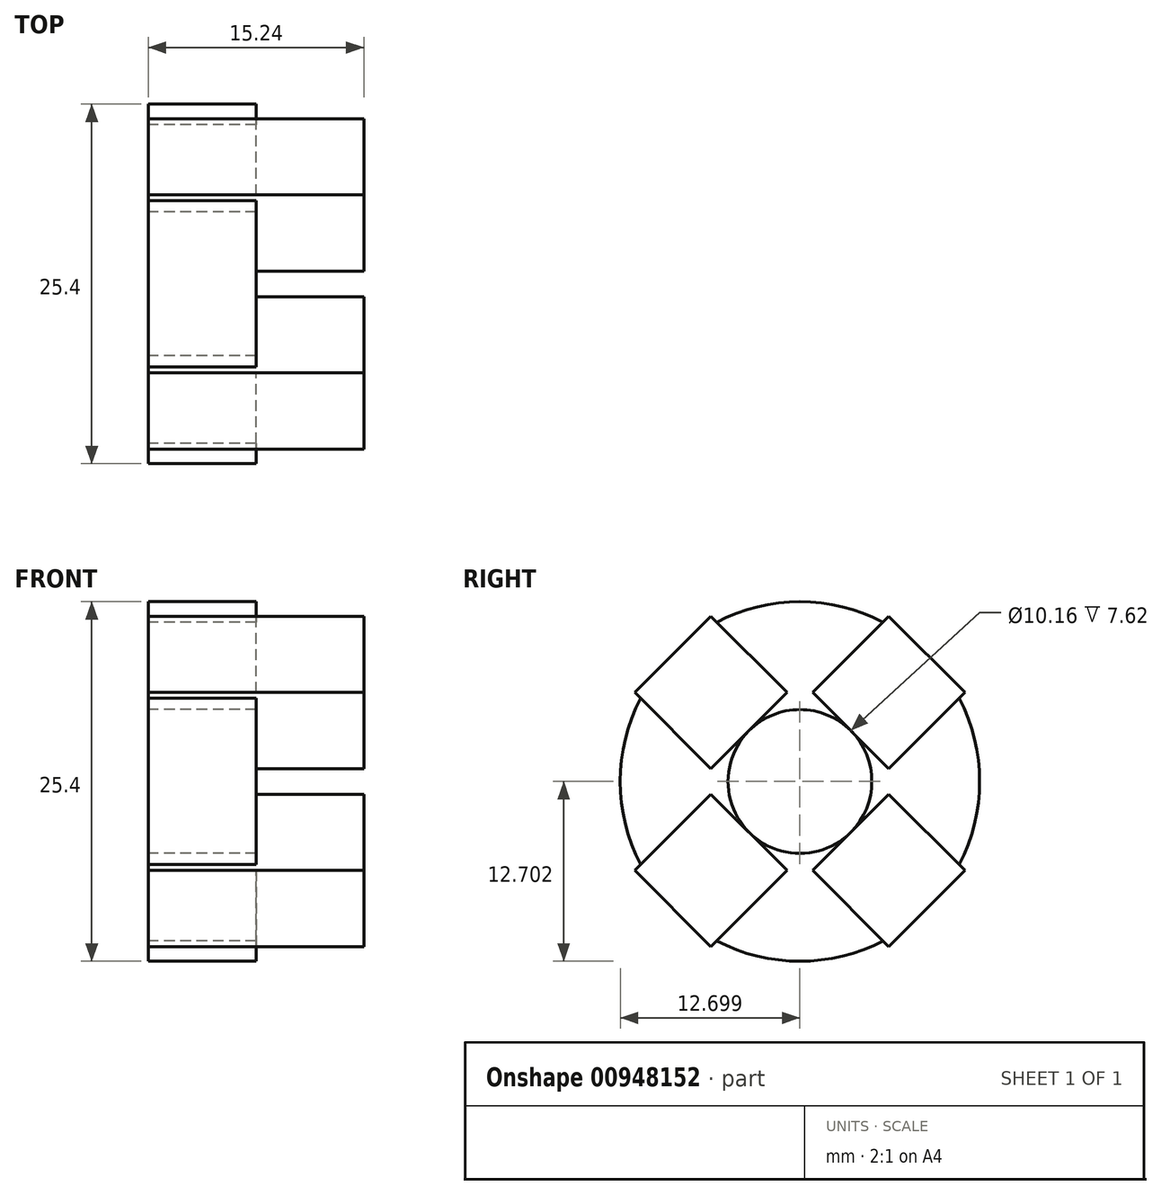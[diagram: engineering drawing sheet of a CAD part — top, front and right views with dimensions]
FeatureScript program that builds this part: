
annotation { "Feature Type Name" : "Feature", "Feature Type Description" : "" }
export const myFeature = defineFeature(function(context is Context, id is Id, definition is map)
    precondition{}
    {
        {
            var Q0;
            Q0=qCreatedBy(makeId("Right.planeOp"),FACE);
            var sketch = newSketch(context, id + "F0", { "sketchPlane" : qUnion([Q0])});
            skCircle(sketch, "E0", {"center": v(-34.03, 25.2) * mm, "radius": 12.7 * mm});
            skCircle(sketch, "E1", {"center": v(-34.03, 25.2) * mm, "radius": 5.08 * mm});
            skLineSegment(sketch, "E2.bottom", {"start": v(-25.05, 34.17) * mm, "end": v(-43.01, 34.17) * mm});
            skLineSegment(sketch, "E2.top", {"start": v(-25.05, 16.21) * mm, "end": v(-43.01, 16.21) * mm});
            skLineSegment(sketch, "E2.left", {"start": v(-25.05, 34.17) * mm, "end": v(-25.05, 16.21) * mm});
            skLineSegment(sketch, "E2.right", {"start": v(-43.01, 34.17) * mm, "end": v(-43.01, 16.21) * mm});
            skLineSegment(sketch, "E3", {"start": v(-27.74, 36.87) * mm, "end": v(-33.13, 31.48) * mm});
            skLineSegment(sketch, "E4", {"start": v(-33.13, 31.48) * mm, "end": v(-27.74, 26.09) * mm});
            skLineSegment(sketch, "E5", {"start": v(-27.74, 26.09) * mm, "end": v(-22.36, 31.48) * mm});
            skLineSegment(sketch, "E6", {"start": v(-22.36, 18.9) * mm, "end": v(-27.74, 24.3) * mm});
            skLineSegment(sketch, "E7", {"start": v(-27.74, 24.3) * mm, "end": v(-33.13, 18.9) * mm});
            skLineSegment(sketch, "E8", {"start": v(-33.13, 18.9) * mm, "end": v(-27.74, 13.53) * mm});
            skLineSegment(sketch, "E9", {"start": v(-40.32, 36.87) * mm, "end": v(-34.93, 31.48) * mm});
            skLineSegment(sketch, "E10", {"start": v(-34.93, 31.48) * mm, "end": v(-40.32, 26.09) * mm});
            skLineSegment(sketch, "E11", {"start": v(-40.32, 26.09) * mm, "end": v(-45.7, 31.48) * mm});
            skLineSegment(sketch, "E12", {"start": v(-27.74, 36.87) * mm, "end": v(-22.36, 31.48) * mm});
            skLineSegment(sketch, "E13", {"start": v(-40.32, 36.87) * mm, "end": v(-45.7, 31.48) * mm});
            skLineSegment(sketch, "E14", {"start": v(-22.36, 18.9) * mm, "end": v(-27.74, 13.53) * mm});
            skLineSegment(sketch, "E15", {"start": v(-40.33, 13.53) * mm, "end": v(-34.95, 18.9) * mm});
            skLineSegment(sketch, "E16", {"start": v(-34.95, 18.9) * mm, "end": v(-40.33, 24.29) * mm});
            skLineSegment(sketch, "E17", {"start": v(-40.33, 24.29) * mm, "end": v(-45.7, 18.9) * mm});
            skLineSegment(sketch, "E18", {"start": v(-45.7, 18.9) * mm, "end": v(-40.33, 13.53) * mm});
            skSolve(sketch);
        }
        {
            var Q0;
            {var subQ0=sQuery(id+"F0.wireOp",EDGE,"E3");var subQ1=sQuery(id+"F0.wireOp",EDGE,"E0");var subQ2=makeQuery(id+"F0.imprint","INTERSECT",VERTEX,{"derivedFrom":[subQ1,subQ0]});Q0=makeQuery(id+"F0.imprint","IMPRINT",FACE,{"disambiguationData":[TD([[makeQuery(id+"F0.imprint","IMPRINT",EDGE,{"disambiguationData":[TD([[subQ2,-1.0]])],"derivedFrom":subQ1}),1.0]])]});}
            var Q1;
            {var subQ7=sQuery(id+"F0.wireOp",EDGE,"E1");var subQ9=sQuery(id+"F0.wireOp",EDGE,"E10");var subQ10=makeQuery(id+"F0.imprint","INTERSECT",VERTEX,{"derivedFrom":[subQ7,subQ9]});Q1=makeQuery(id+"F0.imprint","IMPRINT",FACE,{"disambiguationData":[TD([[makeQuery(id+"F0.imprint","IMPRINT",EDGE,{"disambiguationData":[TD([[subQ10,1.0]])],"derivedFrom":subQ7}),-1.0]])]});}
            var Q2;
            {var subQ0=sQuery(id+"F0.wireOp",EDGE,"E11");var subQ1=sQuery(id+"F0.wireOp",EDGE,"E0");var subQ2=makeQuery(id+"F0.imprint","INTERSECT",VERTEX,{"derivedFrom":[subQ1,subQ0]});Q2=makeQuery(id+"F0.imprint","IMPRINT",FACE,{"disambiguationData":[TD([[makeQuery(id+"F0.imprint","IMPRINT",EDGE,{"disambiguationData":[TD([[subQ2,-1.0]])],"derivedFrom":subQ1}),1.0]])]});}
            var Q3;
            {var subQ17=sQuery(id+"F0.wireOp",EDGE,"E16");Q3=makeQuery(id+"F0.imprint","IMPRINT",FACE,{"disambiguationData":[TD([[makeQuery(id+"F0.imprint","IMPRINT",EDGE,{"derivedFrom":subQ17}),-1.0]])]});}
            var Q4;
            {var subQ1=sQuery(id+"F0.wireOp",EDGE,"E4");var subQ3=sQuery(id+"F0.wireOp",EDGE,"E1");var subQ4=makeQuery(id+"F0.imprint","INTERSECT",VERTEX,{"derivedFrom":[subQ3,subQ1]});Q4=makeQuery(id+"F0.imprint","IMPRINT",FACE,{"disambiguationData":[TD([[makeQuery(id+"F0.imprint","IMPRINT",EDGE,{"disambiguationData":[TD([[subQ4,1.0]])],"derivedFrom":subQ3}),-1.0]])]});}
            var Q5;
            {var subQ0=sQuery(id+"F0.wireOp",EDGE,"E5");var subQ1=sQuery(id+"F0.wireOp",EDGE,"E0");var subQ2=makeQuery(id+"F0.imprint","INTERSECT",VERTEX,{"derivedFrom":[subQ1,subQ0]});Q5=makeQuery(id+"F0.imprint","IMPRINT",FACE,{"disambiguationData":[TD([[makeQuery(id+"F0.imprint","IMPRINT",EDGE,{"disambiguationData":[TD([[subQ2,1.0]])],"derivedFrom":subQ1}),1.0]])]});}
            var Q6;
            {var subQ0=sQuery(id+"F0.wireOp",EDGE,"E15");var subQ1=sQuery(id+"F0.wireOp",EDGE,"E0");var subQ2=makeQuery(id+"F0.imprint","INTERSECT",VERTEX,{"derivedFrom":[subQ1,subQ0]});Q6=makeQuery(id+"F0.imprint","IMPRINT",FACE,{"disambiguationData":[TD([[makeQuery(id+"F0.imprint","IMPRINT",EDGE,{"disambiguationData":[TD([[subQ2,-1.0]])],"derivedFrom":subQ1}),1.0]])]});}
            var Q7;
            {var subQ0=sQuery(id+"F0.wireOp",EDGE,"E10");var subQ1=sQuery(id+"F0.wireOp",EDGE,"E9");var subQ2=makeQuery(id+"F0.imprint","INTERSECT",VERTEX,{"derivedFrom":[subQ1,subQ0]});Q7=makeQuery(id+"F0.imprint","IMPRINT",FACE,{"disambiguationData":[TD([[makeQuery(id+"F0.imprint","IMPRINT",EDGE,{"disambiguationData":[TD([[subQ2,1.0]])],"derivedFrom":subQ1}),-1.0]])]});}
            var Q8;
            {var subQ0=sQuery(id+"F0.wireOp",EDGE,"E13");var subQ1=sQuery(id+"F0.wireOp",EDGE,"E0");var subQ2=makeQuery(id+"F0.imprint","INTERSECT",VERTEX,{"derivedFrom":[subQ1,subQ0]});Q8=makeQuery(id+"F0.imprint","IMPRINT",FACE,{"disambiguationData":[TD([[makeQuery(id+"F0.imprint","IMPRINT",EDGE,{"disambiguationData":[TD([[subQ2,1.0]])],"derivedFrom":subQ1}),1.0]])]});}
            var Q9;
            {var subQ1=sQuery(id+"F0.wireOp",EDGE,"E0");var subQ3=sQuery(id+"F0.wireOp",EDGE,"E11");var subQ4=makeQuery(id+"F0.imprint","INTERSECT",VERTEX,{"derivedFrom":[subQ1,subQ3]});Q9=makeQuery(id+"F0.imprint","IMPRINT",FACE,{"disambiguationData":[TD([[makeQuery(id+"F0.imprint","IMPRINT",EDGE,{"disambiguationData":[TD([[subQ4,1.0]])],"derivedFrom":subQ3}),-1.0]])]});}
            var Q10;
            {var subQ6=sQuery(id+"F0.wireOp",EDGE,"E14");var subQ8=sQuery(id+"F0.wireOp",EDGE,"E2.top");var subQ9=makeQuery(id+"F0.imprint","INTERSECT",VERTEX,{"derivedFrom":[subQ8,subQ6]});Q10=makeQuery(id+"F0.imprint","IMPRINT",FACE,{"disambiguationData":[TD([[makeQuery(id+"F0.imprint","IMPRINT",EDGE,{"disambiguationData":[TD([[subQ9,-1.0]])],"derivedFrom":subQ8}),-1.0]])]});}
            var Q11;
            {var subQ0=sQuery(id+"F0.wireOp",EDGE,"E14");var subQ1=sQuery(id+"F0.wireOp",EDGE,"E0");var subQ2=makeQuery(id+"F0.imprint","INTERSECT",VERTEX,{"disambiguationData":[OD(1.0)],"derivedFrom":[subQ1,subQ0]});Q11=makeQuery(id+"F0.imprint","IMPRINT",FACE,{"disambiguationData":[TD([[makeQuery(id+"F0.imprint","IMPRINT",EDGE,{"disambiguationData":[TD([[subQ2,-1.0]])],"derivedFrom":subQ1}),1.0]])]});}
            var Q12;
            {var subQ0=sQuery(id+"F0.wireOp",EDGE,"E8");var subQ1=sQuery(id+"F0.wireOp",EDGE,"E0");var subQ2=makeQuery(id+"F0.imprint","INTERSECT",VERTEX,{"derivedFrom":[subQ1,subQ0]});Q12=makeQuery(id+"F0.imprint","IMPRINT",FACE,{"disambiguationData":[TD([[makeQuery(id+"F0.imprint","IMPRINT",EDGE,{"disambiguationData":[TD([[subQ2,-1.0]])],"derivedFrom":subQ1}),1.0]])]});}
            var Q13;
            {var subQ0=sQuery(id+"F0.wireOp",EDGE,"E16");Q13=makeQuery(id+"F0.imprint","IMPRINT",FACE,{"disambiguationData":[TD([[makeQuery(id+"F0.imprint","IMPRINT",EDGE,{"derivedFrom":subQ0}),1.0]])]});}
            var Q14;
            {var subQ1=sQuery(id+"F0.wireOp",EDGE,"E0");var subQ3=sQuery(id+"F0.wireOp",EDGE,"E17");var subQ4=makeQuery(id+"F0.imprint","INTERSECT",VERTEX,{"derivedFrom":[subQ1,subQ3]});Q14=makeQuery(id+"F0.imprint","IMPRINT",FACE,{"disambiguationData":[TD([[makeQuery(id+"F0.imprint","IMPRINT",EDGE,{"disambiguationData":[TD([[subQ4,1.0]])],"derivedFrom":subQ3}),1.0]])]});}
            var Q15;
            {var subQ1=sQuery(id+"F0.wireOp",EDGE,"E0");var subQ3=sQuery(id+"F0.wireOp",EDGE,"E15");var subQ4=makeQuery(id+"F0.imprint","INTERSECT",VERTEX,{"derivedFrom":[subQ1,subQ3]});Q15=makeQuery(id+"F0.imprint","IMPRINT",FACE,{"disambiguationData":[TD([[makeQuery(id+"F0.imprint","IMPRINT",EDGE,{"disambiguationData":[TD([[subQ4,-1.0]])],"derivedFrom":subQ3}),1.0]])]});}
            var Q16;
            {var subQ0=sQuery(id+"F0.wireOp",EDGE,"E4");var subQ1=sQuery(id+"F0.wireOp",EDGE,"E3");var subQ2=makeQuery(id+"F0.imprint","INTERSECT",VERTEX,{"derivedFrom":[subQ1,subQ0]});Q16=makeQuery(id+"F0.imprint","IMPRINT",FACE,{"disambiguationData":[TD([[makeQuery(id+"F0.imprint","IMPRINT",EDGE,{"disambiguationData":[TD([[subQ2,1.0]])],"derivedFrom":subQ1}),1.0]])]});}
            var Q17;
            {var subQ1=sQuery(id+"F0.wireOp",EDGE,"E0");var subQ3=sQuery(id+"F0.wireOp",EDGE,"E3");var subQ4=makeQuery(id+"F0.imprint","INTERSECT",VERTEX,{"derivedFrom":[subQ1,subQ3]});Q17=makeQuery(id+"F0.imprint","IMPRINT",FACE,{"disambiguationData":[TD([[makeQuery(id+"F0.imprint","IMPRINT",EDGE,{"disambiguationData":[TD([[subQ4,-1.0]])],"derivedFrom":subQ3}),1.0]])]});}
            var Q18;
            {var subQ1=sQuery(id+"F0.wireOp",EDGE,"E0");var subQ3=sQuery(id+"F0.wireOp",EDGE,"E5");var subQ4=makeQuery(id+"F0.imprint","INTERSECT",VERTEX,{"derivedFrom":[subQ1,subQ3]});Q18=makeQuery(id+"F0.imprint","IMPRINT",FACE,{"disambiguationData":[TD([[makeQuery(id+"F0.imprint","IMPRINT",EDGE,{"disambiguationData":[TD([[subQ4,1.0]])],"derivedFrom":subQ3}),1.0]])]});}
            extrude(context, id + "F1", {"entities" : qUnion([Q0, Q1, Q2, Q3, Q4, Q5, Q6, Q7, Q8, Q9, Q10, Q11, Q12, Q13, Q14, Q15, Q16, Q17, Q18]), "depth" : 7.62 * mm, "offsetDistance" : 25.4 * mm});
        }
        {
            var Q0;
            {var subQ0=sQuery(id+"F0.wireOp",EDGE,"E18");Q0=makeQuery(id+"F0.imprint","IMPRINT",FACE,{"disambiguationData":[TD([[makeQuery(id+"F0.imprint","IMPRINT",EDGE,{"derivedFrom":subQ0}),1.0]])]});}
            var Q1;
            {var subQ1=sQuery(id+"F0.wireOp",EDGE,"E0");var subQ3=sQuery(id+"F0.wireOp",EDGE,"E17");var subQ4=makeQuery(id+"F0.imprint","INTERSECT",VERTEX,{"derivedFrom":[subQ1,subQ3]});Q1=makeQuery(id+"F0.imprint","IMPRINT",FACE,{"disambiguationData":[TD([[makeQuery(id+"F0.imprint","IMPRINT",EDGE,{"disambiguationData":[TD([[subQ4,1.0]])],"derivedFrom":subQ3}),1.0]])]});}
            var Q2;
            {var subQ0=sQuery(id+"F0.wireOp",EDGE,"E16");Q2=makeQuery(id+"F0.imprint","IMPRINT",FACE,{"disambiguationData":[TD([[makeQuery(id+"F0.imprint","IMPRINT",EDGE,{"derivedFrom":subQ0}),1.0]])]});}
            var Q3;
            {var subQ1=sQuery(id+"F0.wireOp",EDGE,"E0");var subQ3=sQuery(id+"F0.wireOp",EDGE,"E15");var subQ4=makeQuery(id+"F0.imprint","INTERSECT",VERTEX,{"derivedFrom":[subQ1,subQ3]});Q3=makeQuery(id+"F0.imprint","IMPRINT",FACE,{"disambiguationData":[TD([[makeQuery(id+"F0.imprint","IMPRINT",EDGE,{"disambiguationData":[TD([[subQ4,-1.0]])],"derivedFrom":subQ3}),1.0]])]});}
            var Q4;
            {var subQ6=sQuery(id+"F0.wireOp",EDGE,"E14");var subQ8=sQuery(id+"F0.wireOp",EDGE,"E2.top");var subQ9=makeQuery(id+"F0.imprint","INTERSECT",VERTEX,{"derivedFrom":[subQ8,subQ6]});Q4=makeQuery(id+"F0.imprint","IMPRINT",FACE,{"disambiguationData":[TD([[makeQuery(id+"F0.imprint","IMPRINT",EDGE,{"disambiguationData":[TD([[subQ9,-1.0]])],"derivedFrom":subQ8}),-1.0]])]});}
            var Q5;
            {var subQ0=sQuery(id+"F0.wireOp",EDGE,"E10");var subQ1=sQuery(id+"F0.wireOp",EDGE,"E9");var subQ2=makeQuery(id+"F0.imprint","INTERSECT",VERTEX,{"derivedFrom":[subQ1,subQ0]});Q5=makeQuery(id+"F0.imprint","IMPRINT",FACE,{"disambiguationData":[TD([[makeQuery(id+"F0.imprint","IMPRINT",EDGE,{"disambiguationData":[TD([[subQ2,1.0]])],"derivedFrom":subQ1}),-1.0]])]});}
            var Q6;
            {var subQ0=sQuery(id+"F0.wireOp",EDGE,"E4");var subQ1=sQuery(id+"F0.wireOp",EDGE,"E3");var subQ2=makeQuery(id+"F0.imprint","INTERSECT",VERTEX,{"derivedFrom":[subQ1,subQ0]});Q6=makeQuery(id+"F0.imprint","IMPRINT",FACE,{"disambiguationData":[TD([[makeQuery(id+"F0.imprint","IMPRINT",EDGE,{"disambiguationData":[TD([[subQ2,1.0]])],"derivedFrom":subQ1}),1.0]])]});}
            var Q7;
            {var subQ1=sQuery(id+"F0.wireOp",EDGE,"E0");var subQ3=sQuery(id+"F0.wireOp",EDGE,"E11");var subQ4=makeQuery(id+"F0.imprint","INTERSECT",VERTEX,{"derivedFrom":[subQ1,subQ3]});Q7=makeQuery(id+"F0.imprint","IMPRINT",FACE,{"disambiguationData":[TD([[makeQuery(id+"F0.imprint","IMPRINT",EDGE,{"disambiguationData":[TD([[subQ4,1.0]])],"derivedFrom":subQ3}),-1.0]])]});}
            var Q8;
            {var subQ0=sQuery(id+"F0.wireOp",EDGE,"E13");var subQ3=sQuery(id+"F0.wireOp",EDGE,"E11");var subQ5=makeQuery(id+"F0.imprint","INTERSECT",VERTEX,{"derivedFrom":[subQ3,subQ0]});Q8=makeQuery(id+"F0.imprint","IMPRINT",FACE,{"disambiguationData":[TD([[makeQuery(id+"F0.imprint","IMPRINT",EDGE,{"disambiguationData":[TD([[subQ5,1.0]])],"derivedFrom":subQ3}),-1.0]])]});}
            var Q9;
            {var subQ0=sQuery(id+"F0.wireOp",EDGE,"E13");var subQ1=sQuery(id+"F0.wireOp",EDGE,"E0");var subQ2=makeQuery(id+"F0.imprint","INTERSECT",VERTEX,{"derivedFrom":[subQ1,subQ0]});Q9=makeQuery(id+"F0.imprint","IMPRINT",FACE,{"disambiguationData":[TD([[makeQuery(id+"F0.imprint","IMPRINT",EDGE,{"disambiguationData":[TD([[subQ2,1.0]])],"derivedFrom":subQ1}),1.0]])]});}
            var Q10;
            {var subQ0=sQuery(id+"F0.wireOp",EDGE,"E13");var subQ1=sQuery(id+"F0.wireOp",EDGE,"E0");var subQ2=makeQuery(id+"F0.imprint","INTERSECT",VERTEX,{"derivedFrom":[subQ1,subQ0]});Q10=makeQuery(id+"F0.imprint","IMPRINT",FACE,{"disambiguationData":[TD([[makeQuery(id+"F0.imprint","IMPRINT",EDGE,{"disambiguationData":[TD([[subQ2,1.0]])],"derivedFrom":subQ1}),-1.0]])]});}
            var Q11;
            {var subQ1=sQuery(id+"F0.wireOp",EDGE,"E0");var subQ3=sQuery(id+"F0.wireOp",EDGE,"E5");var subQ4=makeQuery(id+"F0.imprint","INTERSECT",VERTEX,{"derivedFrom":[subQ1,subQ3]});Q11=makeQuery(id+"F0.imprint","IMPRINT",FACE,{"disambiguationData":[TD([[makeQuery(id+"F0.imprint","IMPRINT",EDGE,{"disambiguationData":[TD([[subQ4,1.0]])],"derivedFrom":subQ3}),1.0]])]});}
            var Q12;
            {var subQ1=sQuery(id+"F0.wireOp",EDGE,"E0");var subQ3=sQuery(id+"F0.wireOp",EDGE,"E3");var subQ4=makeQuery(id+"F0.imprint","INTERSECT",VERTEX,{"derivedFrom":[subQ1,subQ3]});Q12=makeQuery(id+"F0.imprint","IMPRINT",FACE,{"disambiguationData":[TD([[makeQuery(id+"F0.imprint","IMPRINT",EDGE,{"disambiguationData":[TD([[subQ4,-1.0]])],"derivedFrom":subQ3}),1.0]])]});}
            var Q13;
            {var subQ0=sQuery(id+"F0.wireOp",EDGE,"E12");var subQ3=sQuery(id+"F0.wireOp",EDGE,"E3");var subQ5=makeQuery(id+"F0.imprint","INTERSECT",VERTEX,{"derivedFrom":[subQ3,subQ0]});Q13=makeQuery(id+"F0.imprint","IMPRINT",FACE,{"disambiguationData":[TD([[makeQuery(id+"F0.imprint","IMPRINT",EDGE,{"disambiguationData":[TD([[subQ5,-1.0]])],"derivedFrom":subQ3}),1.0]])]});}
            var Q14;
            {var subQ0=sQuery(id+"F0.wireOp",EDGE,"E12");var subQ3=sQuery(id+"F0.wireOp",EDGE,"E5");var subQ5=makeQuery(id+"F0.imprint","INTERSECT",VERTEX,{"derivedFrom":[subQ3,subQ0]});Q14=makeQuery(id+"F0.imprint","IMPRINT",FACE,{"disambiguationData":[TD([[makeQuery(id+"F0.imprint","IMPRINT",EDGE,{"disambiguationData":[TD([[subQ5,1.0]])],"derivedFrom":subQ3}),1.0]])]});}
            var Q15;
            {var subQ0=sQuery(id+"F0.wireOp",EDGE,"E14");var subQ1=sQuery(id+"F0.wireOp",EDGE,"E0");var subQ2=makeQuery(id+"F0.imprint","INTERSECT",VERTEX,{"disambiguationData":[OD(1.0)],"derivedFrom":[subQ1,subQ0]});Q15=makeQuery(id+"F0.imprint","IMPRINT",FACE,{"disambiguationData":[TD([[makeQuery(id+"F0.imprint","IMPRINT",EDGE,{"disambiguationData":[TD([[subQ2,-1.0]])],"derivedFrom":subQ1}),1.0]])]});}
            var Q16;
            {var subQ0=sQuery(id+"F0.wireOp",EDGE,"E8");var subQ1=sQuery(id+"F0.wireOp",EDGE,"E0");var subQ2=makeQuery(id+"F0.imprint","INTERSECT",VERTEX,{"derivedFrom":[subQ1,subQ0]});Q16=makeQuery(id+"F0.imprint","IMPRINT",FACE,{"disambiguationData":[TD([[makeQuery(id+"F0.imprint","IMPRINT",EDGE,{"disambiguationData":[TD([[subQ2,-1.0]])],"derivedFrom":subQ1}),1.0]])]});}
            var Q17;
            {var subQ0=sQuery(id+"F0.wireOp",EDGE,"E14");var subQ1=sQuery(id+"F0.wireOp",EDGE,"E0");var subQ2=makeQuery(id+"F0.imprint","INTERSECT",VERTEX,{"disambiguationData":[OD(1.0)],"derivedFrom":[subQ1,subQ0]});Q17=makeQuery(id+"F0.imprint","IMPRINT",FACE,{"disambiguationData":[TD([[makeQuery(id+"F0.imprint","IMPRINT",EDGE,{"disambiguationData":[TD([[subQ2,-1.0]])],"derivedFrom":subQ1}),-1.0]])]});}
            var Q18;
            {var subQ0=sQuery(id+"F0.wireOp",EDGE,"E8");var subQ1=sQuery(id+"F0.wireOp",EDGE,"E0");var subQ2=makeQuery(id+"F0.imprint","INTERSECT",VERTEX,{"derivedFrom":[subQ1,subQ0]});Q18=makeQuery(id+"F0.imprint","IMPRINT",FACE,{"disambiguationData":[TD([[makeQuery(id+"F0.imprint","IMPRINT",EDGE,{"disambiguationData":[TD([[subQ2,-1.0]])],"derivedFrom":subQ1}),-1.0]])]});}
            extrude(context, id + "F2", {"entities" : qUnion([Q0, Q1, Q2, Q3, Q4, Q5, Q6, Q7, Q8, Q9, Q10, Q11, Q12, Q13, Q14, Q15, Q16, Q17, Q18]), "operationType" : NewBodyOperationType.ADD, "depth" : 15.24 * mm, "offsetDistance" : 25.4 * mm});
        }
    });
